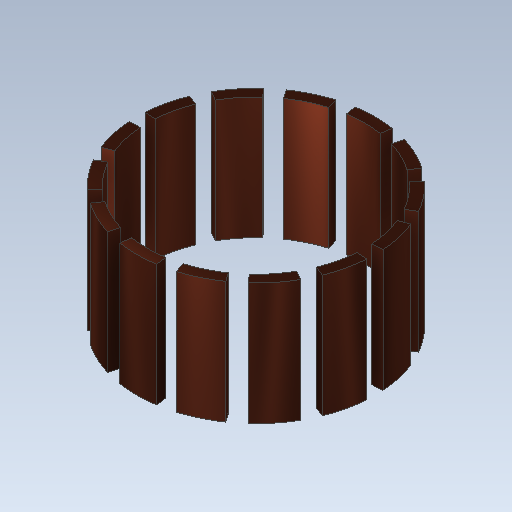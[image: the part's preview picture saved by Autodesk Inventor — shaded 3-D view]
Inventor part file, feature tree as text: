
AUTODESK INVENTOR PART (.ipt)
format: ipt  version: 2020.1 (Build 241239000, 239)  size: 205,312 bytes
history: native  units: mm
features: plane x1
ambient origin geometry x8: Origin, YZ Plane, XZ Plane, XY Plane, X Axis, Y Axis, Z Axis, Center Point
bodies: Solid1 (feature_tree), Solid2 (feature_tree), Solid3 (feature_tree), Solid4 (feature_tree), Solid5 (feature_tree), Solid6 (feature_tree), Solid7 (feature_tree), Solid8 (feature_tree), Solid9 (feature_tree), Solid10 (feature_tree), Solid11 (feature_tree), Solid12 (feature_tree), Solid13 (feature_tree), Solid14 (feature_tree), Body15 (feature_tree), Body16 (feature_tree), Body17 (feature_tree), Body18 (feature_tree), Body19 (feature_tree), Body20 (feature_tree), Body21 (feature_tree), Body22 (feature_tree), Body23 (feature_tree), Body24 (feature_tree), Body25 (feature_tree), Body26 (feature_tree), Body27 (feature_tree), Body28 (feature_tree)
feature tree (1):
  plane  "Work Plane1"
